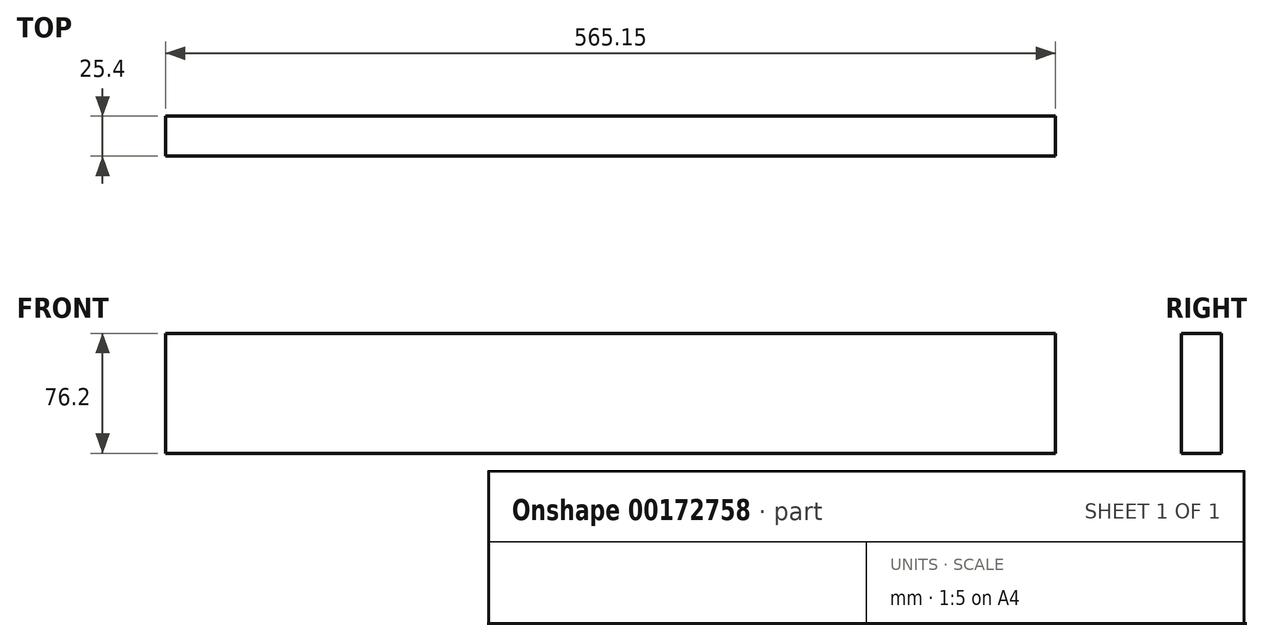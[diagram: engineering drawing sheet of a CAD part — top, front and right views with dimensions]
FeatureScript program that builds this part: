
annotation { "Feature Type Name" : "Feature", "Feature Type Description" : "" }
export const myFeature = defineFeature(function(context is Context, id is Id, definition is map)
    precondition{}
    {
        {
            var Q0;
            Q0=qCreatedBy(makeId("Front.planeOp"),FACE);
            var sketch = newSketch(context, id + "F0", { "sketchPlane" : qUnion([Q0])});
            skLineSegment(sketch, "E0.bottom", {"start": v(-288.54, 0) * mm, "end": v(276.6, 0) * mm});
            skLineSegment(sketch, "E0.top", {"start": v(-288.54, -76.2) * mm, "end": v(276.6, -76.2) * mm});
            skLineSegment(sketch, "E0.left", {"start": v(-288.54, 0) * mm, "end": v(-288.54, -76.2) * mm});
            skLineSegment(sketch, "E0.right", {"start": v(276.6, 0) * mm, "end": v(276.6, -76.2) * mm});
            skSolve(sketch);
        }
        {
            var Q0;
            Q0 = qSketchRegion(id + "F0", true);
            extrude(context, id + "F1", {"entities" : qUnion([Q0]), "depth" : 25.4 * mm});
        }
    });
